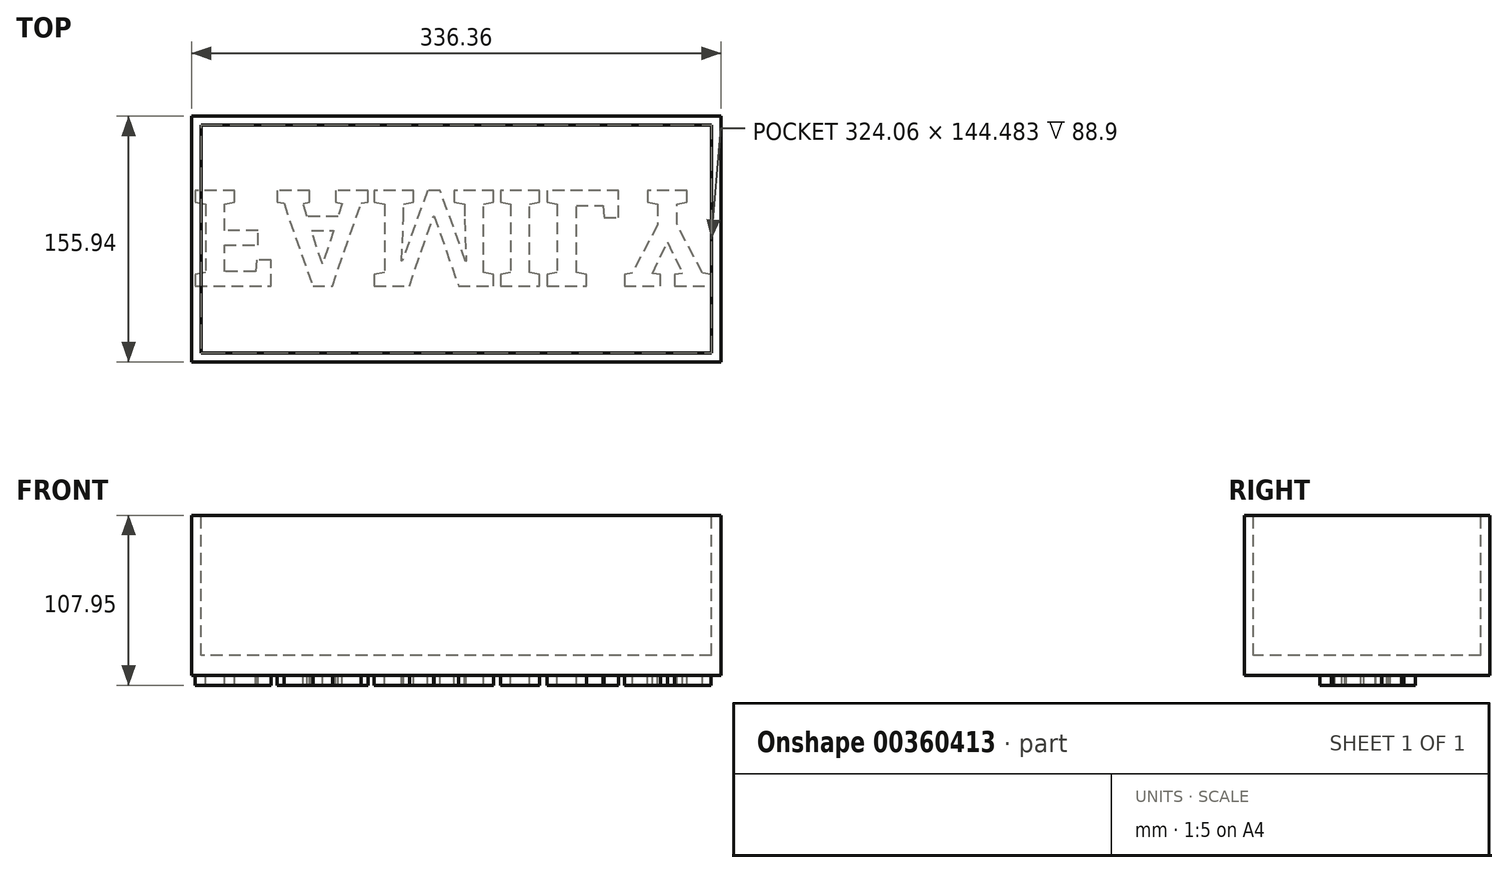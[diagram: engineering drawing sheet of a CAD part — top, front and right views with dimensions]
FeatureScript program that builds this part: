
annotation { "Feature Type Name" : "Feature", "Feature Type Description" : "" }
export const myFeature = defineFeature(function(context is Context, id is Id, definition is map)
    precondition{}
    {
        {
            var Q0;
            Q0=qCreatedBy(makeId("Top.planeOp"),FACE);
            var sketch = newSketch(context, id + "F0", { "sketchPlane" : qUnion([Q0])});
            skLineSegment(sketch, "E0.bottom", {"start": v(168.18, 77.97) * mm, "end": v(-168.18, 77.97) * mm});
            skLineSegment(sketch, "E0.top", {"start": v(168.18, -77.97) * mm, "end": v(-168.18, -77.97) * mm});
            skLineSegment(sketch, "E0.left", {"start": v(168.18, 77.97) * mm, "end": v(168.18, -77.97) * mm});
            skLineSegment(sketch, "E0.right", {"start": v(-168.18, 77.97) * mm, "end": v(-168.18, -77.97) * mm});
            skPoint(sketch, "E0.middle", {"position": v(0, 0) * mm});
            skSolve(sketch);
        }
        {
            var Q0;
            Q0 = qSketchRegion(id + "F0", true);
            extrude(context, id + "F1", {"entities" : qUnion([Q0]), "depth" : 101.6 * mm});
        }
        {
            var Q0;
            Q0=makeQuery(id+"F1.opExtrude","CAP_FACE",FACE,{"disambiguationData":[OSD([sQuery(id+"F0.wireOp",EDGE,"E0.bottom"),sQuery(id+"F0.wireOp",EDGE,"E0.top"),sQuery(id+"F0.wireOp",EDGE,"E0.left"),sQuery(id+"F0.wireOp",EDGE,"E0.right")])],"isStart":false});
            var sketch = newSketch(context, id + "F2", { "sketchPlane" : qUnion([Q0])});
            skLineSegment(sketch, "E1.bottom", {"start": v(162.03, 72.24) * mm, "end": v(-162.03, 72.24) * mm});
            skLineSegment(sketch, "E1.top", {"start": v(162.03, -72.24) * mm, "end": v(-162.03, -72.24) * mm});
            skLineSegment(sketch, "E1.left", {"start": v(162.03, 72.24) * mm, "end": v(162.03, -72.24) * mm});
            skLineSegment(sketch, "E1.right", {"start": v(-162.03, 72.24) * mm, "end": v(-162.03, -72.24) * mm});
            skPoint(sketch, "E1.middle", {"position": v(0, 0) * mm});
            skSolve(sketch);
        }
        {
            var Q0;
            Q0 = qSketchRegion(id + "F2", true);
            extrude(context, id + "F3", {"entities" : qUnion([Q0]), "operationType" : NewBodyOperationType.REMOVE, "oppositeDirection" : true, "depth" : 88.9 * mm});
        }
        {
            var Q0;
            Q0=makeQuery(id+"F1.opExtrude","CAP_FACE",FACE,{"disambiguationData":[OSD([sQuery(id+"F0.wireOp",EDGE,"E0.bottom"),sQuery(id+"F0.wireOp",EDGE,"E0.top"),sQuery(id+"F0.wireOp",EDGE,"E0.left"),sQuery(id+"F0.wireOp",EDGE,"E0.right")])],"isStart":true});
            var sketch = newSketch(context, id + "F4", { "sketchPlane" : qUnion([Q0])});
            skText(sketch, "E2", { "text": "FAMILY", "fontName": "RobotoSlab-Bold.ttf"});
            const initialGuessF4  = {"E2": [-0.16818, -0.03064, 1, 0, 0.06126]};
            skSetInitialGuess(sketch, initialGuessF4);
            skSolve(sketch);
        }
        {
            var Q0;
            Q0 = qSketchRegion(id + "F4", true);
            extrude(context, id + "F5", {"entities" : qUnion([Q0]), "operationType" : NewBodyOperationType.ADD, "depth" : 6.35 * mm});
        }
    });
